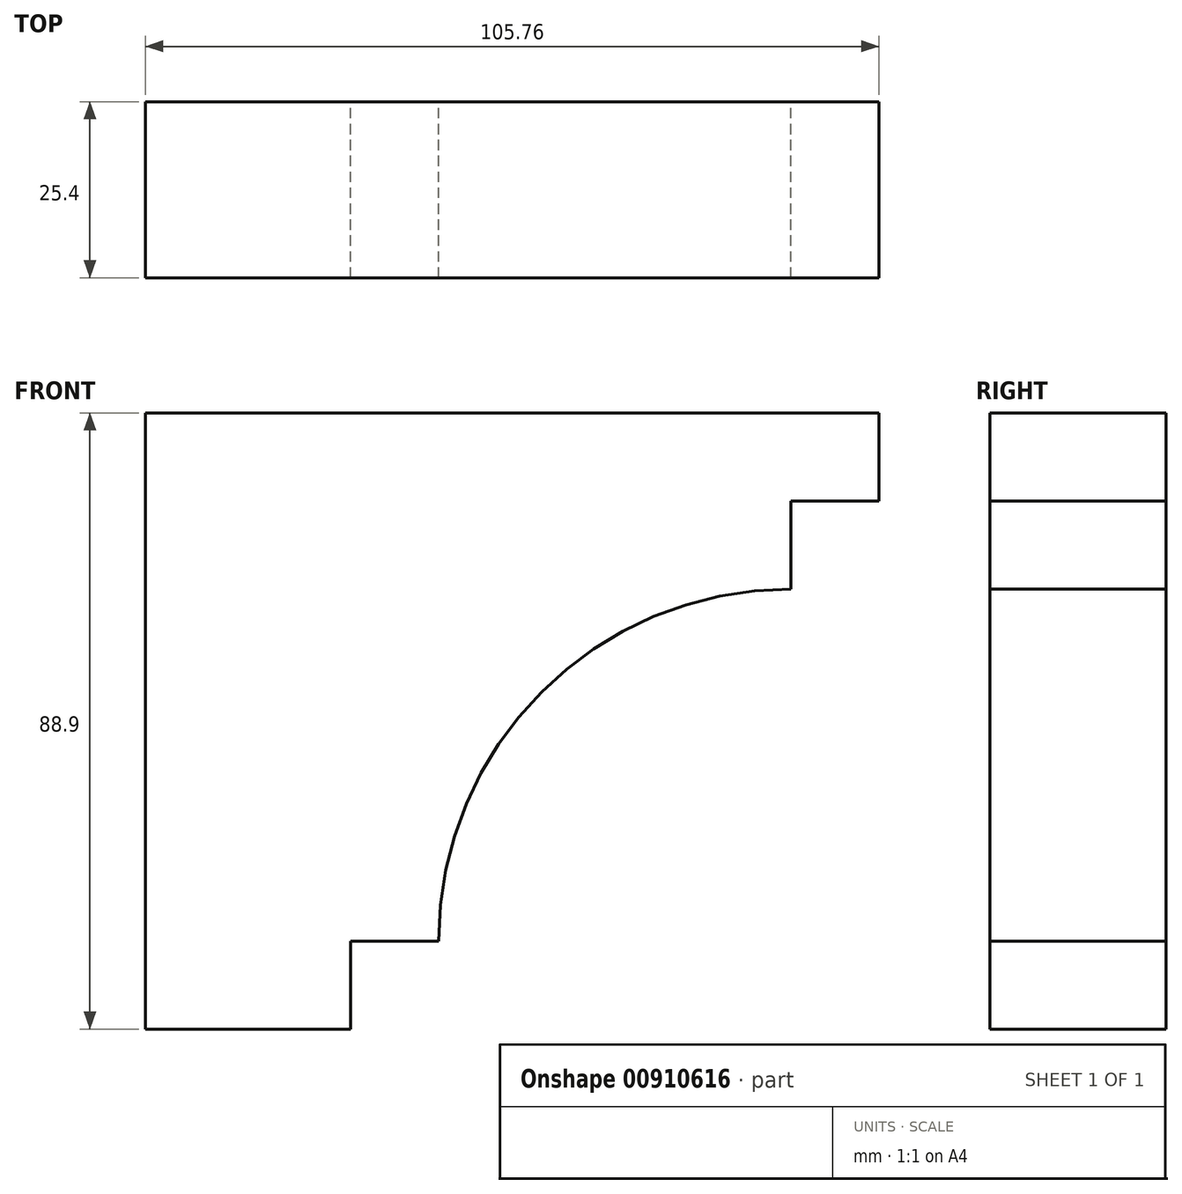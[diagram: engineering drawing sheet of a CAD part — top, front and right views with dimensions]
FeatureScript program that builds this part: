
annotation { "Feature Type Name" : "Feature", "Feature Type Description" : "" }
export const myFeature = defineFeature(function(context is Context, id is Id, definition is map)
    precondition{}
    {
        {
            var Q0;
            Q0=qCreatedBy(makeId("Front.planeOp"),FACE);
            var sketch = newSketch(context, id + "F0", { "sketchPlane" : qUnion([Q0])});
            skLineSegment(sketch, "E0", {"start": v(0, 0) * mm, "end": v(105.76, 0) * mm});
            skLineSegment(sketch, "E1", {"start": v(105.76, 0) * mm, "end": v(105.76, -12.7) * mm});
            skLineSegment(sketch, "E2", {"start": v(0, 0) * mm, "end": v(0, -88.9) * mm});
            skLineSegment(sketch, "E3", {"start": v(0, -88.9) * mm, "end": v(29.56, -88.9) * mm});
            skLineSegment(sketch, "E4", {"start": v(29.56, -88.9) * mm, "end": v(29.56, -76.2) * mm});
            skLineSegment(sketch, "E5", {"start": v(29.56, -76.2) * mm, "end": v(42.26, -76.2) * mm});
            skArc(sketch, "E6", {"start": v(93.06, -25.4) * mm, "mid": v(57.14, -40.28) * mm, "end": v(42.26, -76.2) * mm});
            skLineSegment(sketch, "E7", {"start": v(42.26, -76.2) * mm, "end": v(42.26, -103.34) * mm, "construction": true});
            skLineSegment(sketch, "E8", {"start": v(93.06, -25.4) * mm, "end": v(93.06, -12.7) * mm});
            skLineSegment(sketch, "E9", {"start": v(93.06, -12.7) * mm, "end": v(105.76, -12.7) * mm});
            skLineSegment(sketch, "E10", {"start": v(93.06, -25.4) * mm, "end": v(111.48, -25.4) * mm, "construction": true});
            skSolve(sketch);
        }
        {
            var Q0;
            Q0 = qSketchRegion(id + "F0", true);
            extrude(context, id + "F1", {"entities" : qUnion([Q0]), "depth" : 25.4 * mm, "offsetDistance" : 25.4 * mm});
        }
    });
